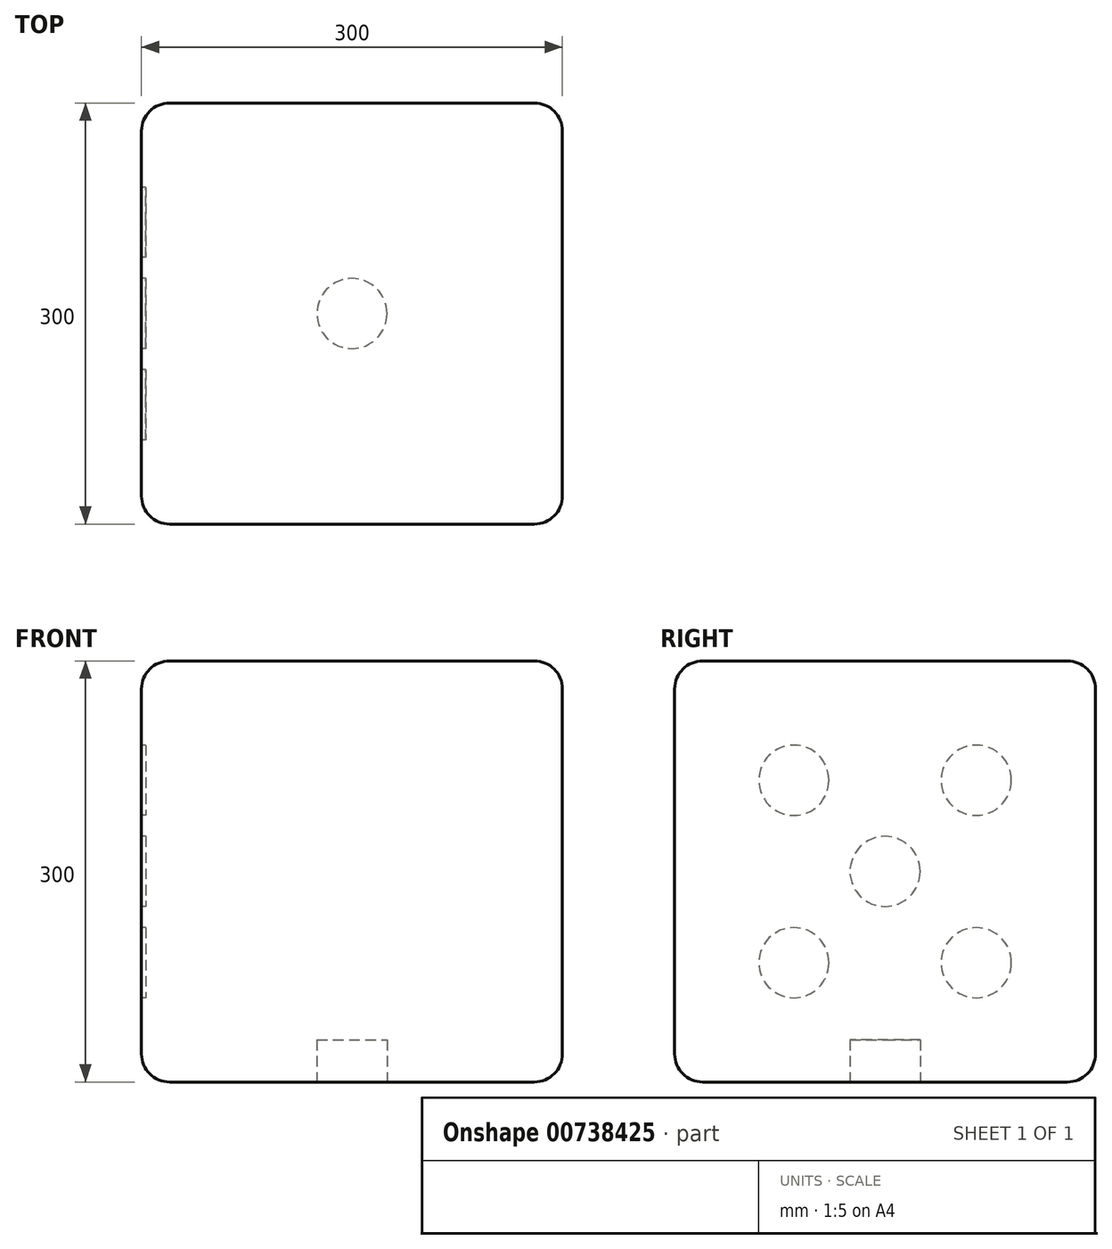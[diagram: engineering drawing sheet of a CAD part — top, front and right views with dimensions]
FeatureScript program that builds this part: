
annotation { "Feature Type Name" : "Feature", "Feature Type Description" : "" }
export const myFeature = defineFeature(function(context is Context, id is Id, definition is map)
    precondition{}
    {
        {
            var Q0;
            Q0=qCreatedBy(makeId("Top.planeOp"),FACE);
            var sketch = newSketch(context, id + "F0", { "sketchPlane" : qUnion([Q0])});
            skLineSegment(sketch, "E0.bottom", {"start": v(-214.88, 150.72) * mm, "end": v(85.12, 150.72) * mm});
            skLineSegment(sketch, "E0.top", {"start": v(-214.88, -149.28) * mm, "end": v(85.12, -149.28) * mm});
            skLineSegment(sketch, "E0.left", {"start": v(-214.88, 150.72) * mm, "end": v(-214.88, -149.28) * mm});
            skLineSegment(sketch, "E0.right", {"start": v(85.12, 150.72) * mm, "end": v(85.12, -149.28) * mm});
            skSolve(sketch);
        }
        {
            var Q0;
            Q0=makeQuery(id+"F0.imprint","IMPRINT",FACE,{"disambiguationData":[TD([[makeQuery(id+"F0.imprint","IMPRINT",EDGE,{"derivedFrom":sQuery(id+"F0.wireOp",EDGE,"E0.bottom")}),-1.0]])]});
            extrude(context, id + "F1", {"entities" : qUnion([Q0]), "depth" : 300 * mm, "offsetDistance" : 25 * mm});
        }
        {
            var Q0;
            Q0=makeQuery(id+"F1.opExtrude","SWEPT_EDGE",EDGE,{"disambiguationData":[OSD([sQuery(id+"F0.wireOp",EDGE,"E0.bottom"),sQuery(id+"F0.wireOp",EDGE,"E0.left")])]});
            var Q1;
            Q1=makeQuery(id+"F1.opExtrude","CAP_EDGE",EDGE,{"disambiguationData":[OSD([sQuery(id+"F0.wireOp",EDGE,"E0.bottom")])],"isStart":false});
            var Q2;
            Q2=makeQuery(id+"F1.opExtrude","CAP_EDGE",EDGE,{"disambiguationData":[OSD([sQuery(id+"F0.wireOp",EDGE,"E0.left")])],"isStart":false});
            var Q3;
            Q3=makeQuery(id+"F1.opExtrude","CAP_FACE",FACE,{"disambiguationData":[OSD([sQuery(id+"F0.wireOp",EDGE,"E0.bottom"),sQuery(id+"F0.wireOp",EDGE,"E0.top"),sQuery(id+"F0.wireOp",EDGE,"E0.left"),sQuery(id+"F0.wireOp",EDGE,"E0.right")])],"isStart":true});
            var Q4;
            Q4=makeQuery(id+"F1.opExtrude","SWEPT_EDGE",EDGE,{"disambiguationData":[OSD([sQuery(id+"F0.wireOp",EDGE,"E0.bottom"),sQuery(id+"F0.wireOp",EDGE,"E0.right")])]});
            var Q5;
            Q5=makeQuery(id+"F1.opExtrude","SWEPT_EDGE",EDGE,{"disambiguationData":[OSD([sQuery(id+"F0.wireOp",EDGE,"E0.top"),sQuery(id+"F0.wireOp",EDGE,"E0.left")])]});
            var Q6;
            Q6=makeQuery(id+"F1.opExtrude","SWEPT_FACE",FACE,{"disambiguationData":[OSD([sQuery(id+"F0.wireOp",EDGE,"E0.top")])]});
            var Q7;
            Q7=makeQuery(id+"F1.opExtrude","CAP_EDGE",EDGE,{"disambiguationData":[OSD([sQuery(id+"F0.wireOp",EDGE,"E0.right")])],"isStart":false});
            fillet(context, id + "F2", {"entities" : qUnion([Q0, Q1, Q2, Q3, Q4, Q5, Q6, Q7]), "radius" : 20 * mm, "tangentPropagation" : true, "allowEdgeOverflow" : false});
        }
        {
            var Q0;
            Q0=makeQuery(id+"F1.opExtrude","CAP_FACE",FACE,{"disambiguationData":[OSD([sQuery(id+"F0.wireOp",EDGE,"E0.bottom"),sQuery(id+"F0.wireOp",EDGE,"E0.top"),sQuery(id+"F0.wireOp",EDGE,"E0.left"),sQuery(id+"F0.wireOp",EDGE,"E0.right")])],"isStart":true});
            var sketch = newSketch(context, id + "F3", { "sketchPlane" : qUnion([Q0])});
            skLineSegment(sketch, "E1", {"start": v(-64.88, 129.28) * mm, "end": v(-64.88, -130.72) * mm, "construction": true});
            skLineSegment(sketch, "E2", {"start": v(-194.88, -0.72) * mm, "end": v(65.12, -0.72) * mm, "construction": true});
            skCircle(sketch, "E3", {"center": v(-64.88, -0.72) * mm, "radius": 25 * mm});
            skSolve(sketch);
        }
        {
            var Q0;
            Q0 = qSketchRegion(id + "F3", true);
            extrude(context, id + "F4", {"entities" : qUnion([Q0]), "operationType" : NewBodyOperationType.REMOVE, "oppositeDirection" : true, "depth" : 30 * mm, "offsetDistance" : 25 * mm});
        }
        {
            var Q0;
            Q0=makeQuery(id+"F1.opExtrude","SWEPT_FACE",FACE,{"disambiguationData":[OSD([sQuery(id+"F0.wireOp",EDGE,"E0.left")])]});
            var sketch = newSketch(context, id + "F5", { "sketchPlane" : qUnion([Q0])});
            skLineSegment(sketch, "E4", {"start": v(-0.72, 280) * mm, "end": v(-0.72, 20) * mm, "construction": true});
            skLineSegment(sketch, "E5", {"start": v(129.28, 150) * mm, "end": v(-130.72, 150) * mm, "construction": true});
            skLineSegment(sketch, "E6", {"start": v(129.28, 280) * mm, "end": v(129.28, 150) * mm, "construction": true});
            skLineSegment(sketch, "E7", {"start": v(129.28, 215) * mm, "end": v(-0.72, 215) * mm, "construction": true});
            skLineSegment(sketch, "E8", {"start": v(-0.72, 215) * mm, "end": v(-130.72, 215) * mm, "construction": true});
            skLineSegment(sketch, "E9", {"start": v(-130.72, 150) * mm, "end": v(-130.72, 20) * mm, "construction": true});
            skLineSegment(sketch, "E10", {"start": v(-130.72, 85) * mm, "end": v(129.28, 85) * mm, "construction": true});
            skLineSegment(sketch, "E11", {"start": v(129.28, 20) * mm, "end": v(-0.72, 20) * mm, "construction": true});
            skLineSegment(sketch, "E12", {"start": v(-130.72, 20) * mm, "end": v(-0.72, 20) * mm, "construction": true});
            skLineSegment(sketch, "E13", {"start": v(64.28, 20) * mm, "end": v(64.28, 280) * mm, "construction": true});
            skLineSegment(sketch, "E14", {"start": v(-65.72, 20) * mm, "end": v(-65.72, 280) * mm, "construction": true});
            skCircle(sketch, "E15", {"center": v(64.28, 215) * mm, "radius": 25 * mm});
            skCircle(sketch, "E16", {"center": v(64.28, 85) * mm, "radius": 25 * mm});
            skCircle(sketch, "E17", {"center": v(-65.72, 85) * mm, "radius": 25 * mm});
            skCircle(sketch, "E18", {"center": v(-65.72, 215) * mm, "radius": 25 * mm});
            skCircle(sketch, "E19", {"center": v(-0.72, 150) * mm, "radius": 25 * mm});
            skSolve(sketch);
        }
        {
            var Q0;
            Q0=makeQuery(id+"F5.imprint","IMPRINT",FACE,{"disambiguationData":[TD([[makeQuery(id+"F5.imprint","IMPRINT",EDGE,{"derivedFrom":sQuery(id+"F5.wireOp",EDGE,"E15")}),1.0]])]});
            var Q1;
            Q1=makeQuery(id+"F5.imprint","IMPRINT",FACE,{"disambiguationData":[TD([[makeQuery(id+"F5.imprint","IMPRINT",EDGE,{"derivedFrom":sQuery(id+"F5.wireOp",EDGE,"E19")}),1.0]])]});
            var Q2;
            Q2=makeQuery(id+"F5.imprint","IMPRINT",FACE,{"disambiguationData":[TD([[makeQuery(id+"F5.imprint","IMPRINT",EDGE,{"derivedFrom":sQuery(id+"F5.wireOp",EDGE,"E16")}),1.0]])]});
            var Q3;
            Q3=makeQuery(id+"F5.imprint","IMPRINT",FACE,{"disambiguationData":[TD([[makeQuery(id+"F5.imprint","IMPRINT",EDGE,{"derivedFrom":sQuery(id+"F5.wireOp",EDGE,"E17")}),1.0]])]});
            var Q4;
            Q4=makeQuery(id+"F5.imprint","IMPRINT",FACE,{"disambiguationData":[TD([[makeQuery(id+"F5.imprint","IMPRINT",EDGE,{"derivedFrom":sQuery(id+"F5.wireOp",EDGE,"E18")}),1.0]])]});
            extrude(context, id + "F6", {"entities" : qUnion([Q0, Q1, Q2, Q3, Q4]), "operationType" : NewBodyOperationType.REMOVE, "oppositeDirection" : true, "depth" : 3 * mm, "offsetDistance" : 25 * mm});
        }
    });
